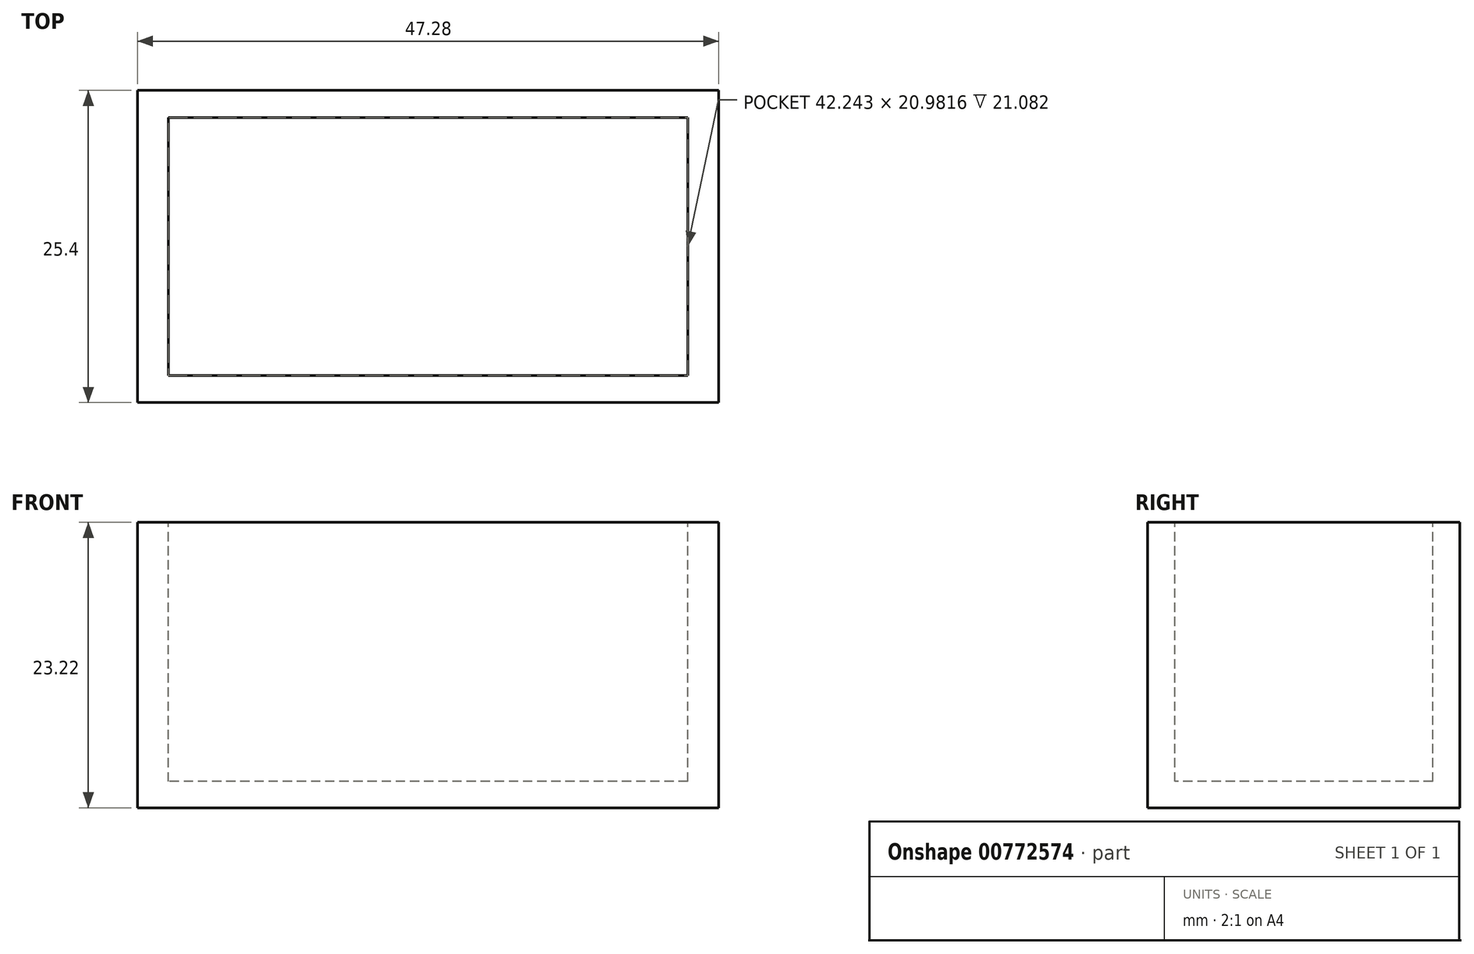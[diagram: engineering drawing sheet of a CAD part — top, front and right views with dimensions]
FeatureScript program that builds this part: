
annotation { "Feature Type Name" : "Feature", "Feature Type Description" : "" }
export const myFeature = defineFeature(function(context is Context, id is Id, definition is map)
    precondition{}
    {
        {
            var Q0;
            Q0=qCreatedBy(makeId("Front.planeOp"),FACE);
            var sketch = newSketch(context, id + "F0", { "sketchPlane" : qUnion([Q0])});
            skLineSegment(sketch, "E0.bottom", {"start": v(23.64, 11.6) * mm, "end": v(-23.64, 11.6) * mm});
            skLineSegment(sketch, "E0.top", {"start": v(23.64, -11.6) * mm, "end": v(-23.64, -11.6) * mm});
            skLineSegment(sketch, "E0.left", {"start": v(23.64, 11.6) * mm, "end": v(23.64, -11.6) * mm});
            skLineSegment(sketch, "E0.right", {"start": v(-23.64, 11.6) * mm, "end": v(-23.64, -11.6) * mm});
            skPoint(sketch, "E0.middle", {"position": v(0, 0) * mm});
            skSolve(sketch);
        }
        {
            var Q0;
            Q0=makeQuery(id+"F0.imprint","IMPRINT",FACE,{"disambiguationData":[TD([[makeQuery(id+"F0.imprint","IMPRINT",EDGE,{"derivedFrom":sQuery(id+"F0.wireOp",EDGE,"E0.bottom")}),1.0]])]});
            extrude(context, id + "F1", {"entities" : qUnion([Q0]), "depth" : 12.7 * mm, "offsetDistance" : 25.4 * mm, "hasSecondDirection" : true, "secondDirectionOppositeDirection" : true, "secondDirectionDepth" : 12.7 * mm});
        }
        {
            var Q0;
            Q0=makeQuery(id+"F1.opExtrude","SWEPT_FACE",FACE,{"disambiguationData":[OSD([sQuery(id+"F0.wireOp",EDGE,"E0.bottom")])]});
            var sketch = newSketch(context, id + "F2", { "sketchPlane" : qUnion([Q0])});
            skLineSegment(sketch, "E1.bottom", {"start": v(21.12, 10.5) * mm, "end": v(-21.12, 10.5) * mm});
            skLineSegment(sketch, "E1.top", {"start": v(21.12, -10.5) * mm, "end": v(-21.12, -10.5) * mm});
            skLineSegment(sketch, "E1.left", {"start": v(21.12, 10.5) * mm, "end": v(21.12, -10.5) * mm});
            skLineSegment(sketch, "E1.right", {"start": v(-21.12, 10.5) * mm, "end": v(-21.12, -10.5) * mm});
            skPoint(sketch, "E1.middle", {"position": v(0, 0) * mm});
            skSolve(sketch);
        }
        {
            var Q0;
            Q0=makeQuery(id+"F2.imprint","IMPRINT",FACE,{"disambiguationData":[TD([[makeQuery(id+"F2.imprint","IMPRINT",EDGE,{"derivedFrom":sQuery(id+"F2.wireOp",EDGE,"E1.bottom")}),1.0]])]});
            extrude(context, id + "F3", {"entities" : qUnion([Q0]), "operationType" : NewBodyOperationType.REMOVE, "oppositeDirection" : true, "depth" : 21.08 * mm, "offsetDistance" : 25.4 * mm});
        }
    });
